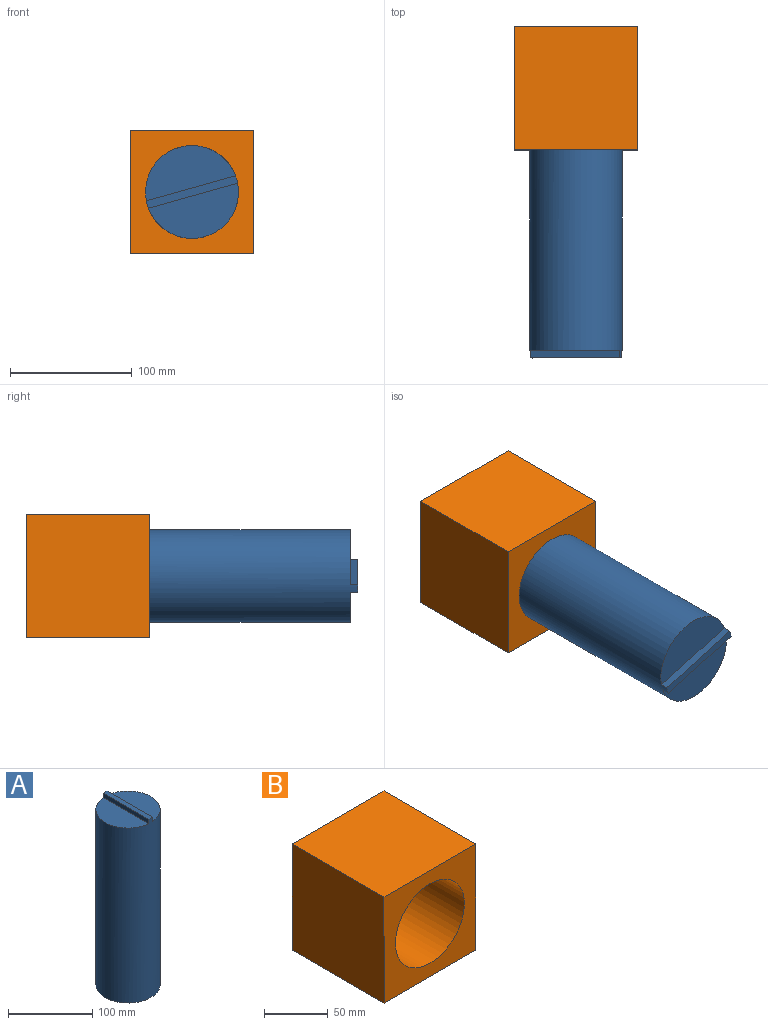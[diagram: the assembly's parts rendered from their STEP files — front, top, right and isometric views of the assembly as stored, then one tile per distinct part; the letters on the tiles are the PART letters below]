
ASSEMBLY  parts=2 mates=1
PART A: 7 faces, bbox 76.2x76.2x260.4 mm
  f0: plane 75.94x34.93mm, normal (0,0,1), area 2038.5mm2, adj f1,f5
  f1: cylinder r=38.1mm len=260.35mm, axis (0,0,-1), area 60885.6mm2, adj f0,f2,f3,f4,f5,f6
  f2: plane 75.94x34.93mm, normal (0,0,1), area 2038.5mm2, adj f1,f4
  f3: plane 76.2x76.2mm, normal (0,0,-1), area 4560.4mm2, adj f1
  f4: plane 75.94x6.35mm, normal (-1,0,0), area 482.2mm2, adj f1,f2,f6
  f5: plane 75.94x6.35mm, normal (1,0,0), area 482.2mm2, adj f0,f1,f6
  f6: plane 76.2x6.35mm, normal (0,0,1), area 483.3mm2, adj f1,f4,f5
PART B: 7 faces, bbox 101.6x101.6x101.6 mm
  f0: plane 101.6x101.6mm, normal (-1,0,0), area 10322.6mm2, adj f1,f3,f5,f6
  f1: plane 101.6x101.6mm, normal (0,0,-1), area 10322.6mm2, adj f0,f2,f5,f6
  f2: plane 101.6x101.6mm, normal (1,0,0), area 10322.6mm2, adj f1,f3,f5,f6
  f3: plane 101.6x101.6mm, normal (0,0,1), area 10322.6mm2, adj f0,f2,f5,f6
  f4: cylinder r=38.1mm len=101.6mm, axis (0,1,0), area 24322mm2, adj f5,f6
  f5: plane 101.6x101.6mm, normal (0,-1,0), area 5762.2mm2, adj f0,f1,f2,f3,f4
  f6: plane 101.6x101.6mm, normal (0,1,0), area 5762.2mm2, adj f0,f1,f2,f3,f4
PLACE A rot(axis=(0.68,0.52,-0.52),111.4deg) t=(0,38.84,50.8)mm
PLACE B t=(-50.8,50.8,0)mm
MATE cylindrical A.f1 <-> B.f4  axis (0,1,0) through (0,-91.34,50.8)mm
